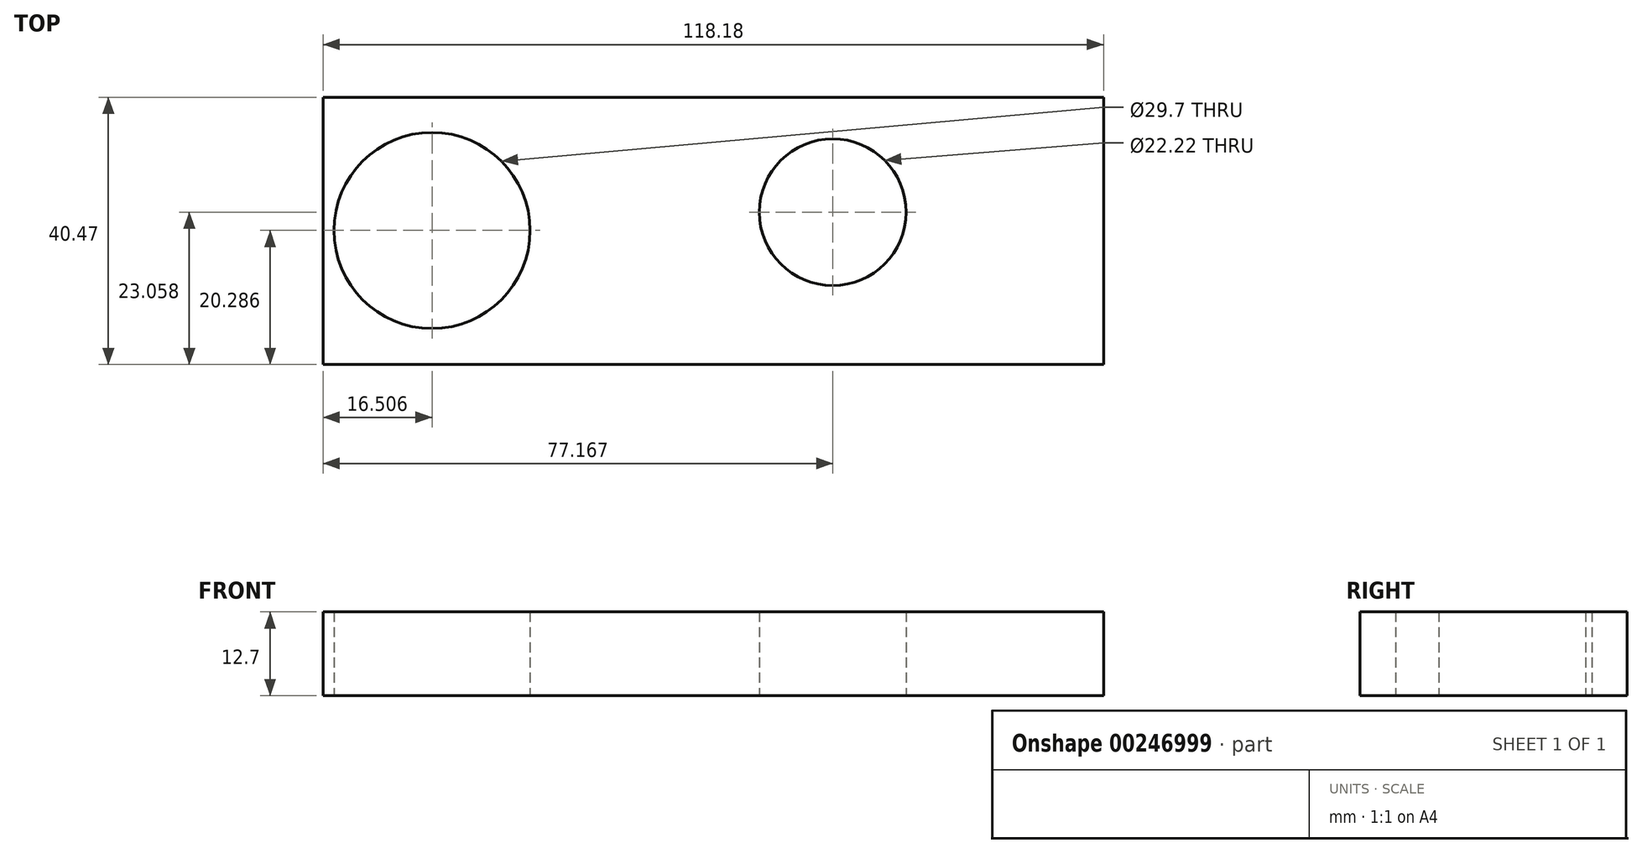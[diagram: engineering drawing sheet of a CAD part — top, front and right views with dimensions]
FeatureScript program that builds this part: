
annotation { "Feature Type Name" : "Feature", "Feature Type Description" : "" }
export const myFeature = defineFeature(function(context is Context, id is Id, definition is map)
    precondition{}
    {
        {
            var Q0;
            Q0=qCreatedBy(makeId("Top.planeOp"),FACE);
            var sketch = newSketch(context, id + "F0", { "sketchPlane" : qUnion([Q0])});
            skLineSegment(sketch, "E0.bottom", {"start": v(-62.34, -35.55) * mm, "end": v(55.84, -35.55) * mm});
            skLineSegment(sketch, "E0.top", {"start": v(-62.34, 4.92) * mm, "end": v(55.84, 4.92) * mm});
            skLineSegment(sketch, "E0.left", {"start": v(-62.34, -35.55) * mm, "end": v(-62.34, 4.92) * mm});
            skLineSegment(sketch, "E0.right", {"start": v(55.84, -35.55) * mm, "end": v(55.84, 4.92) * mm});
            skCircle(sketch, "E1", {"center": v(-45.83, -15.26) * mm, "radius": 14.85 * mm});
            skCircle(sketch, "E2", {"center": v(14.83, -12.5) * mm, "radius": 11.1 * mm});
            skSolve(sketch);
        }
        {
            var Q0;
            Q0=makeQuery(id+"F0.imprint","IMPRINT",FACE,{"disambiguationData":[TD([[makeQuery(id+"F0.imprint","IMPRINT",EDGE,{"derivedFrom":sQuery(id+"F0.wireOp",EDGE,"E0.bottom")}),1.0]])]});
            extrude(context, id + "F1", {"entities" : qUnion([Q0]), "depth" : 12.7 * mm});
        }
    });
